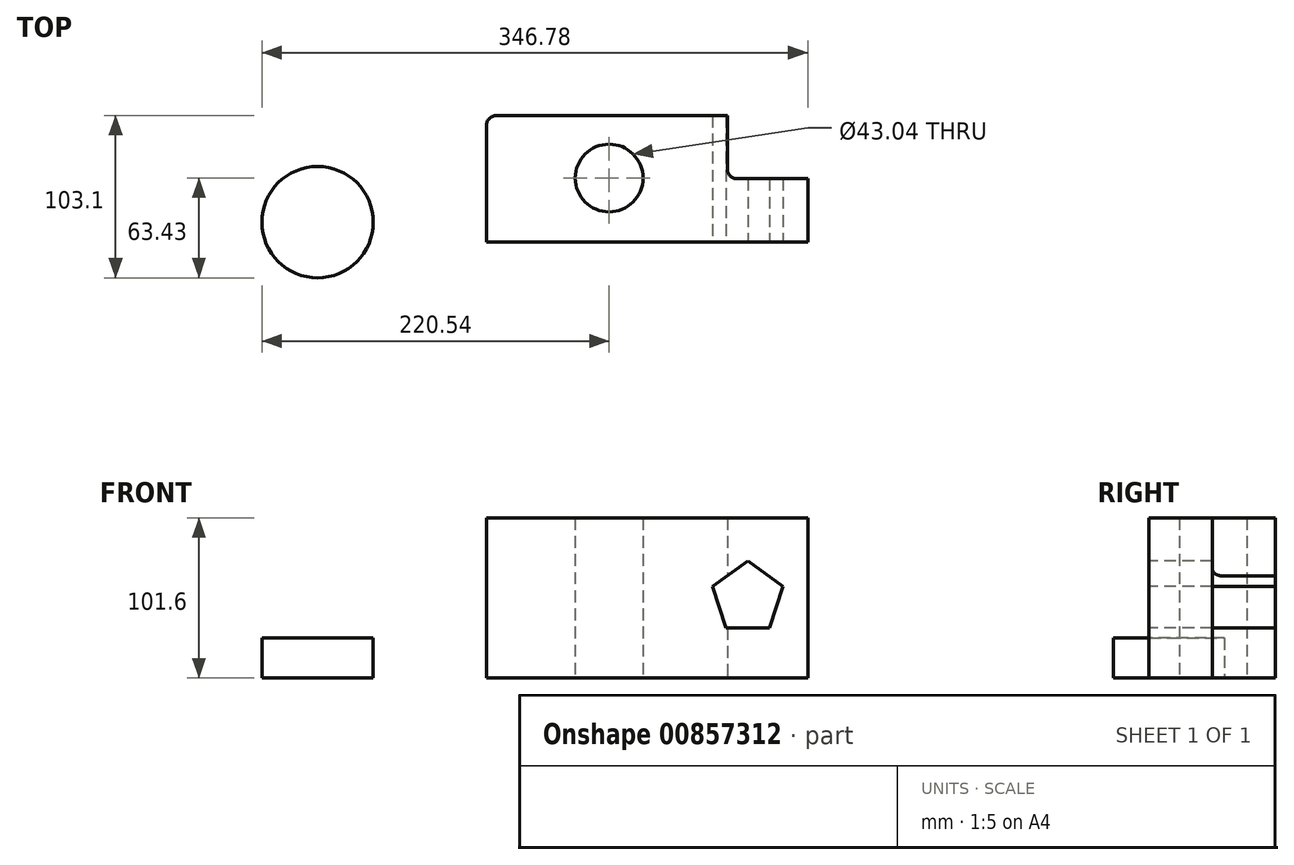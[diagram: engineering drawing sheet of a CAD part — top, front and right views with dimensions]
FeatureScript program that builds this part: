
annotation { "Feature Type Name" : "Feature", "Feature Type Description" : "" }
export const myFeature = defineFeature(function(context is Context, id is Id, definition is map)
    precondition{}
    {
        {
            var Q0;
            Q0=qCreatedBy(makeId("Top.planeOp"),FACE);
            var sketch = newSketch(context, id + "F0", { "sketchPlane" : qUnion([Q0])});
            skLineSegment(sketch, "E0.bottom", {"start": v(-71.56, 39.67) * mm, "end": v(75.05, 39.67) * mm});
            skLineSegment(sketch, "E0.top", {"start": v(-77.91, -40.62) * mm, "end": v(75.05, -40.62) * mm});
            skLineSegment(sketch, "E0.left", {"start": v(-77.91, 33.32) * mm, "end": v(-77.91, -40.62) * mm});
            skLineSegment(sketch, "E0.right", {"start": v(75.05, 39.67) * mm, "end": v(75.05, 5.87) * mm});
            skCircle(sketch, "E1", {"center": v(0, 0) * mm, "radius": 21.52 * mm});
            skPoint(sketch, "E2.visualSharp", {"position": v(-77.91, 39.67) * mm});
            skArc(sketch, "E2.filletArc", {"start": v(-71.56, 39.67) * mm, "mid": v(-76.05, 37.81) * mm, "end": v(-77.91, 33.32) * mm});
            skLineSegment(sketch, "E3", {"start": v(81.4, -0.48) * mm, "end": v(126.24, -0.48) * mm});
            skLineSegment(sketch, "E4", {"start": v(126.24, -0.48) * mm, "end": v(126.24, -40.62) * mm});
            skLineSegment(sketch, "E5", {"start": v(126.24, -40.62) * mm, "end": v(75.05, -40.62) * mm});
            skPoint(sketch, "E6.visualSharp", {"position": v(75.05, -0.48) * mm});
            skArc(sketch, "E6.filletArc", {"start": v(75.05, 5.87) * mm, "mid": v(76.91, 1.38) * mm, "end": v(81.4, -0.48) * mm});
            skSolve(sketch);
        }
        {
            var Q0;
            Q0 = qSketchRegion(id + "F0", true);
            extrude(context, id + "F1", {"entities" : qUnion([Q0]), "depth" : 101.6 * mm, "offsetDistance" : 25.4 * mm});
        }
        {
            var Q0;
            Q0=makeQuery(id+"F1.opExtrude","SWEPT_FACE",FACE,{"disambiguationData":[OSD([sQuery(id+"F0.wireOp",EDGE,"E0.top"),sQuery(id+"F0.wireOp",EDGE,"E5")])]});
            var sketch = newSketch(context, id + "F2", { "sketchPlane" : qUnion([Q0])});
            skCircle(sketch, "E7.cCircle", {"center": v(88.14, 50.8) * mm, "radius": 19.05 * mm, "construction": true});
            skLineSegment(sketch, "E7.0", {"start": v(74.3, 31.75) * mm, "end": v(65.75, 58.08) * mm});
            skLineSegment(sketch, "E7.1", {"start": v(65.75, 58.08) * mm, "end": v(88.14, 74.35) * mm});
            skLineSegment(sketch, "E7.2", {"start": v(88.14, 74.35) * mm, "end": v(110.54, 58.08) * mm});
            skLineSegment(sketch, "E7.3", {"start": v(110.54, 58.08) * mm, "end": v(101.98, 31.75) * mm});
            skLineSegment(sketch, "E7.4", {"start": v(101.98, 31.75) * mm, "end": v(74.3, 31.75) * mm});
            skLineSegment(sketch, "E8", {"start": v(65.75, 58.08) * mm, "end": v(88.14, 74.35) * mm, "construction": true});
            skSolve(sketch);
        }
        {
            var Q0;
            Q0 = qSketchRegion(id + "F2", true);
            extrude(context, id + "F3", {"entities" : qUnion([Q0]), "operationType" : NewBodyOperationType.REMOVE, "endBound" : BoundingType.THROUGH_ALL, "oppositeDirection" : true, "depth" : 33.53 * mm, "offsetDistance" : 25.4 * mm});
        }
        {
            var Q0;
            Q0=qCreatedBy(makeId("Top.planeOp"),FACE);
            var sketch = newSketch(context, id + "F4", { "sketchPlane" : qUnion([Q0])});
            skCircle(sketch, "E9", {"center": v(-185.15, -28.04) * mm, "radius": 35.39 * mm});
            skSolve(sketch);
        }
        {
            var Q0;
            Q0 = qSketchRegion(id + "F4", true);
            extrude(context, id + "F5", {"entities" : qUnion([Q0]), "depth" : 25.4 * mm, "offsetDistance" : 25.4 * mm});
        }
    });
